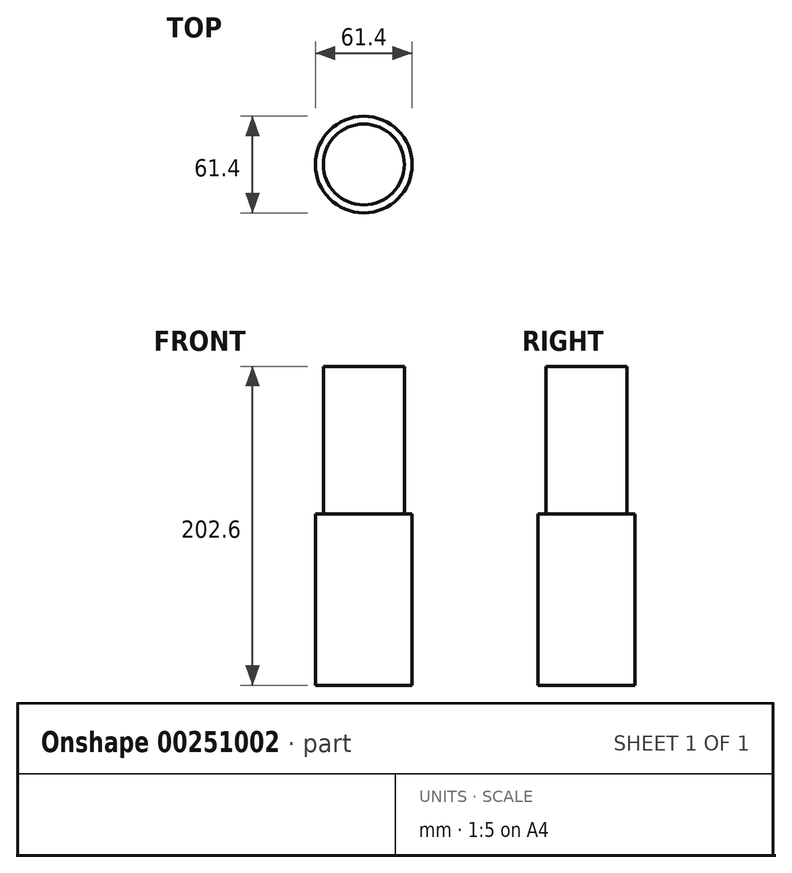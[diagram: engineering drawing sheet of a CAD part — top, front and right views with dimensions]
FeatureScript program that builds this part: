
annotation { "Feature Type Name" : "Feature", "Feature Type Description" : "" }
export const myFeature = defineFeature(function(context is Context, id is Id, definition is map)
    precondition{}
    {
        {
            var Q0;
            Q0=qCreatedBy(makeId("Front.planeOp"),FACE);
            var sketch = newSketch(context, id + "F0", { "sketchPlane" : qUnion([Q0])});
            skLineSegment(sketch, "E0.bottom", {"start": v(-30.7, 54.36) * mm, "end": v(30.7, 54.36) * mm});
            skLineSegment(sketch, "E0.top", {"start": v(-30.7, -54.36) * mm, "end": v(30.7, -54.36) * mm});
            skLineSegment(sketch, "E0.left", {"start": v(-30.7, 54.36) * mm, "end": v(-30.7, -54.36) * mm});
            skLineSegment(sketch, "E0.right", {"start": v(30.7, 54.36) * mm, "end": v(30.7, -54.36) * mm});
            skPoint(sketch, "E0.middle", {"position": v(0, 0) * mm});
            skLineSegment(sketch, "E1", {"start": v(0, 54.36) * mm, "end": v(0, -58.95) * mm});
            skPoint(sketch, "E1.endSnap0", {"position": v(0, -54.36) * mm});
            skSolve(sketch);
        }
        {
            var Q0;
            {var subQ0=sQuery(id+"F0.wireOp",EDGE,"E0.left");Q0=makeQuery(id+"F0.imprint","IMPRINT",FACE,{"disambiguationData":[TD([[makeQuery(id+"F0.imprint","IMPRINT",EDGE,{"derivedFrom":subQ0}),1.0]])]});}
            var Q1;
            Q1=sQuery(id+"F0.wireOp",EDGE,"E1");
            revolve(context, id + "F1", {"entities" : qUnion([Q0]), "axis" : qUnion([Q1]), "revolveType" : RevolveType.FULL});
        }
        {
            var Q0;
            Q0=makeQuery(id+"F1.opRevolve","SWEPT_FACE",FACE,{"disambiguationData":[OSD([sQuery(id+"F0.wireOp",EDGE,"E0.bottom")])]});
            shell(context, id + "F2", {"entities" : qUnion([Q0]), "thickness" : 5 * mm});
        }
        {
            var Q0;
            Q0=makeQuery(id+"F2.opShell","OFFSET_FACE",FACE,{"disambiguationData":[OSD([sQuery(id+"F0.wireOp",EDGE,"E0.top")])]});
            extrude(context, id + "F3", {"entities" : qUnion([Q0]), "operationType" : NewBodyOperationType.ADD, "depth" : 25 * mm});
        }
        {
            var Q0;
            Q0=makeQuery(id+"F3.opExtrude","CAP_FACE",FACE,{"disambiguationData":[OSD([sQuery(id+"F0.wireOp",EDGE,"E0.top")])],"isStart":false});
            extrude(context, id + "F4", {"entities" : qUnion([Q0]), "operationType" : NewBodyOperationType.ADD, "depth" : 172.6 * mm});
        }
    });
